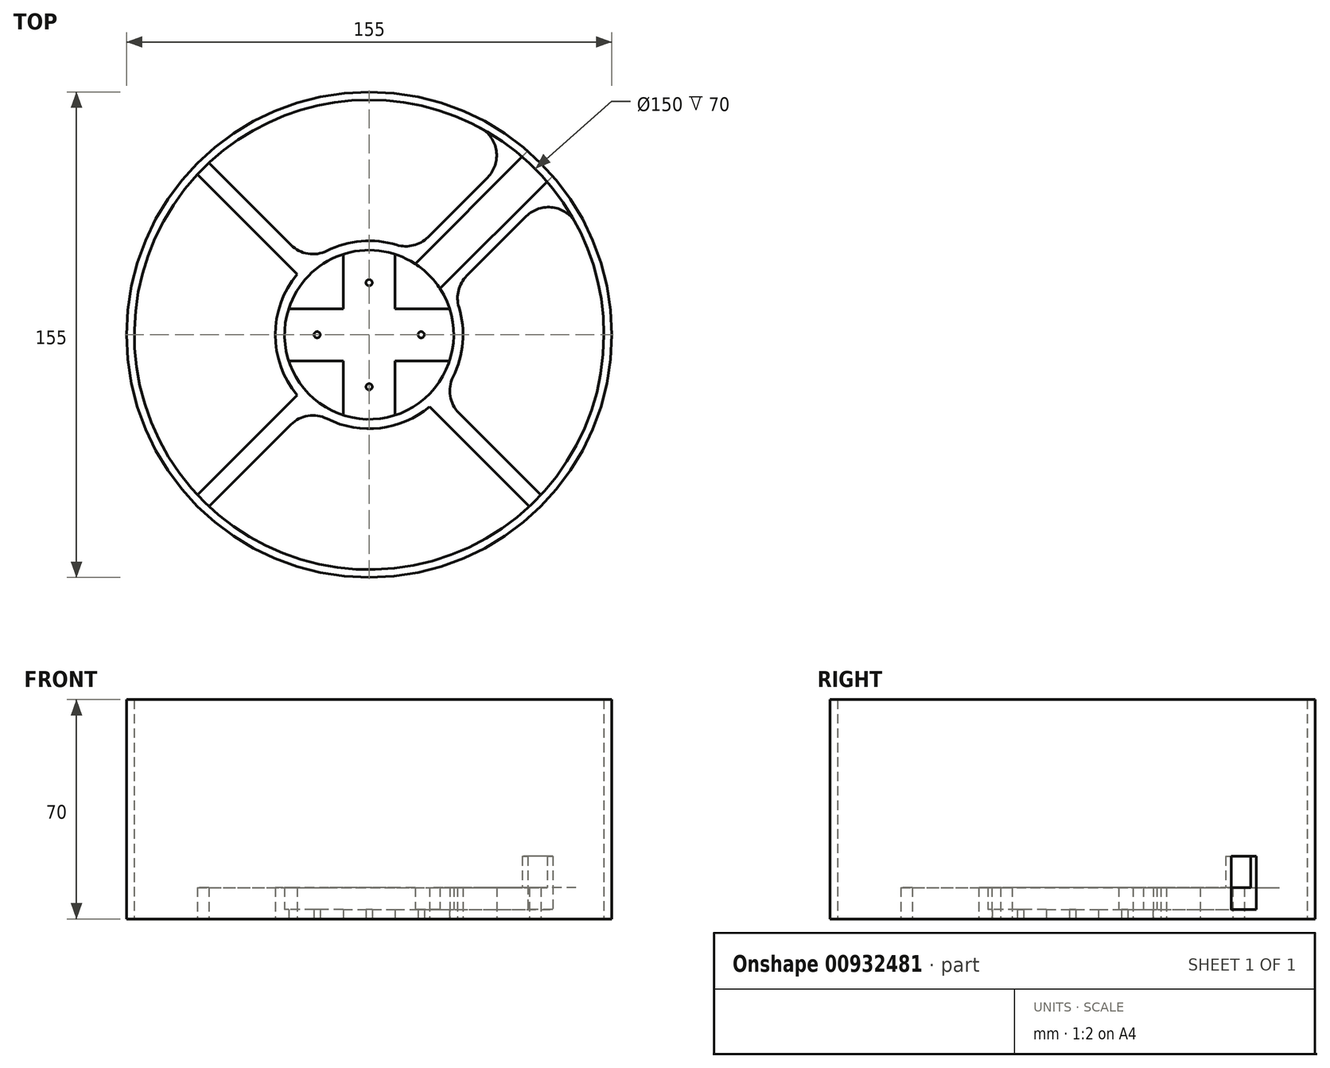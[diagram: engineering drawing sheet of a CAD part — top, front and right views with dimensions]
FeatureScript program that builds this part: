
annotation { "Feature Type Name" : "Feature", "Feature Type Description" : "" }
export const myFeature = defineFeature(function(context is Context, id is Id, definition is map)
    precondition{}
    {
        {
            var Q0;
            Q0=qCreatedBy(makeId("Top.planeOp"),FACE);
            var sketch = newSketch(context, id + "F0", { "sketchPlane" : qUnion([Q0])});
            skCircle(sketch, "E0", {"center": v(0, 0) * mm, "radius": 77.5 * mm});
            skCircle(sketch, "E1", {"center": v(0, 0) * mm, "radius": 75 * mm});
            skSolve(sketch);
        }
        {
            var Q0;
            Q0=qSketchRegion(id+"F0",true);
            var Q1;
            Q1=makeQuery(id+"F0.imprint","IMPRINT",FACE,{"disambiguationData":[TD([[makeQuery(id+"F0.imprint","IMPRINT",EDGE,{"derivedFrom":sQuery(id+"F0.wireOp",EDGE,"E0")}),1.0]])]});
            extrude(context, id + "F1", {"entities" : qUnion([Q0, Q1]), "depth" : 70 * mm, "offsetDistance" : 25 * mm});
        }
        {
            var Q0;
            Q0=qCreatedBy(makeId("Top.planeOp"),FACE);
            var sketch = newSketch(context, id + "F2", { "sketchPlane" : qUnion([Q0])});
            skPoint(sketch, "E2.middle", {"position": v(0, 0) * mm});
            skCircle(sketch, "E3", {"center": v(0, -16.62) * mm, "radius": 1 * mm});
            skCircle(sketch, "E4.0.1.0", {"center": v(16.62, 0) * mm, "radius": 1 * mm});
            skCircle(sketch, "E4.1.0.0", {"center": v(-16.62, 0) * mm, "radius": 1 * mm});
            skCircle(sketch, "E4.1.1.0", {"center": v(0, 16.62) * mm, "radius": 1 * mm});
            skLineSegment(sketch, "E4.direction1", {"start": v(0, -16.62) * mm, "end": v(-16.62, 0) * mm, "construction": true});
            skLineSegment(sketch, "E4.direction2", {"start": v(0, -16.62) * mm, "end": v(16.62, 0) * mm, "construction": true});
            skArc(sketch, "E5", {"start": v(28.83, -8.3) * mm, "mid": v(30, 0) * mm, "end": v(28.83, 8.3) * mm});
            skLineSegment(sketch, "E6", {"start": v(16.62, 0) * mm, "end": v(-16.62, 0) * mm});
            skLineSegment(sketch, "E7", {"start": v(8.3, 8.3) * mm, "end": v(28.83, 8.3) * mm});
            skLineSegment(sketch, "E8.MirrorCS", {"start": v(8.3, 8.3) * mm, "end": v(8.3, 28.83) * mm});
            skLineSegment(sketch, "E9.1.0", {"start": v(-8.3, 8.3) * mm, "end": v(-28.83, 8.3) * mm});
            skLineSegment(sketch, "E9.1.1", {"start": v(-8.3, 8.3) * mm, "end": v(-8.3, 28.83) * mm});
            skLineSegment(sketch, "E9.2.0", {"start": v(-8.3, -8.3) * mm, "end": v(-8.3, -28.83) * mm});
            skLineSegment(sketch, "E9.2.1", {"start": v(-8.3, -8.3) * mm, "end": v(-28.83, -8.3) * mm});
            skLineSegment(sketch, "E10.1.3.0", {"start": v(8.3, -8.3) * mm, "end": v(28.83, -8.3) * mm});
            skLineSegment(sketch, "E10.3.3.0", {"start": v(8.3, -8.3) * mm, "end": v(8.3, -28.83) * mm});
            skArc(sketch, "E11.trimOffspring", {"start": v(8.3, 28.83) * mm, "mid": v(0, 30) * mm, "end": v(-8.3, 28.83) * mm});
            skArc(sketch, "E12.trimOffspring", {"start": v(-28.83, 8.3) * mm, "mid": v(-30, 0) * mm, "end": v(-28.83, -8.3) * mm});
            skArc(sketch, "E13.trimOffspring", {"start": v(-8.3, -28.83) * mm, "mid": v(0, -30) * mm, "end": v(8.3, -28.83) * mm});
            skLineSegment(sketch, "E14.0", {"start": v(-8.3, -8.3) * mm, "end": v(0, -16.62) * mm, "construction": true});
            skLineSegment(sketch, "E14.1", {"start": v(-8.3, -8.3) * mm, "end": v(0, 0) * mm, "construction": true});
            skLineSegment(sketch, "E15.0", {"start": v(0, 16.62) * mm, "end": v(8.3, 8.3) * mm, "construction": true});
            skSolve(sketch);
        }
        {
            var Q0;
            Q0=qSketchRegion(id+"F2",true);
            extrude(context, id + "F3", {"entities" : qUnion([Q0]), "depth" : 3 * mm, "offsetDistance" : 25 * mm});
        }
        {
            var Q0;
            Q0=qCreatedBy(makeId("Top.planeOp"),FACE);
            var sketch = newSketch(context, id + "F4", { "sketchPlane" : qUnion([Q0])});
            skCircle(sketch, "E16", {"center": v(0, 0) * mm, "radius": 30 * mm});
            skCircle(sketch, "E17.0", {"center": v(0, 0) * mm, "radius": 27 * mm});
            skSolve(sketch);
        }
        {
            var Q0;
            Q0=qSketchRegion(id+"F4",true);
            extrude(context, id + "F5", {"entities" : qUnion([Q0]), "operationType" : NewBodyOperationType.ADD, "depth" : 10 * mm, "offsetDistance" : 25 * mm});
        }
        {
            var Q0;
            Q0=qCreatedBy(makeId("Top.planeOp"),FACE);
            var sketch = newSketch(context, id + "F6", { "sketchPlane" : qUnion([Q0])});
            skArc(sketch, "E18", {"start": v(-22.96, -19.3) * mm, "mid": v(-21.21, -21.21) * mm, "end": v(-19.3, -22.96) * mm});
            skArc(sketch, "E19", {"start": v(-54.83, -51.18) * mm, "mid": v(-53.03, -53.03) * mm, "end": v(-51.18, -54.83) * mm});
            skLineSegment(sketch, "E20", {"start": v(-51.18, -54.83) * mm, "end": v(-19.3, -22.96) * mm});
            skLineSegment(sketch, "E21.MirrorCS", {"start": v(-54.83, -51.18) * mm, "end": v(-22.96, -19.3) * mm});
            skPoint(sketch, "E22.center", {"position": v(-2.42, -0.16) * mm});
            skPoint(sketch, "E23", {"position": v(-53.03, -53.03) * mm});
            skPoint(sketch, "E24", {"position": v(-21.21, -21.21) * mm});
            skLineSegment(sketch, "E25", {"start": v(-53.03, -53.03) * mm, "end": v(-21.21, -21.21) * mm, "construction": true});
            skLineSegment(sketch, "E26", {"start": v(-54.83, -51.18) * mm, "end": v(-51.18, -54.83) * mm});
            skLineSegment(sketch, "E27", {"start": v(-22.96, -19.3) * mm, "end": v(-19.3, -22.96) * mm});
            skLineSegment(sketch, "E28", {"start": v(-21.21, -21.21) * mm, "end": v(0, 0) * mm, "construction": true});
            skLineSegment(sketch, "E29.1.0", {"start": v(54.83, -51.18) * mm, "end": v(22.96, -19.3) * mm});
            skLineSegment(sketch, "E29.1.1", {"start": v(53.03, -53.03) * mm, "end": v(21.21, -21.21) * mm, "construction": true});
            skLineSegment(sketch, "E29.1.2", {"start": v(51.18, -54.83) * mm, "end": v(19.3, -22.96) * mm});
            skArc(sketch, "E29.1.3", {"start": v(51.18, -54.83) * mm, "mid": v(53.03, -53.03) * mm, "end": v(54.83, -51.18) * mm});
            skArc(sketch, "E29.1.4", {"start": v(19.3, -22.96) * mm, "mid": v(21.21, -21.21) * mm, "end": v(22.96, -19.3) * mm});
            skLineSegment(sketch, "E29.1.5", {"start": v(21.21, -21.21) * mm, "end": v(0, 0) * mm, "construction": true});
            skLineSegment(sketch, "E30.3.3.0", {"start": v(-53.03, 53.03) * mm, "end": v(-21.21, 21.21) * mm, "construction": true});
            skLineSegment(sketch, "E30.4.3.0", {"start": v(-54.83, 51.18) * mm, "end": v(-22.96, 19.3) * mm});
            skLineSegment(sketch, "E30.6.3.0", {"start": v(-51.18, 54.83) * mm, "end": v(-19.3, 22.96) * mm});
            skArc(sketch, "E30.9.3.0", {"start": v(-51.18, 54.83) * mm, "mid": v(-53.03, 53.03) * mm, "end": v(-54.83, 51.18) * mm});
            skArc(sketch, "E30.13.3.0", {"start": v(-19.3, 22.96) * mm, "mid": v(-21.21, 21.21) * mm, "end": v(-22.96, 19.3) * mm});
            skLineSegment(sketch, "E30.17.3.0", {"start": v(-21.21, 21.21) * mm, "end": v(0, 0) * mm, "construction": true});
            skLineSegment(sketch, "E31", {"start": v(26.42, 14.02) * mm, "end": v(59.73, 47.33) * mm});
            skLineSegment(sketch, "E32.MirrorCS", {"start": v(14.02, 26.42) * mm, "end": v(47.33, 59.73) * mm});
            skLineSegment(sketch, "E33", {"start": v(26.42, 14.02) * mm, "end": v(14.02, 26.42) * mm});
            skLineSegment(sketch, "E34", {"start": v(59.73, 47.33) * mm, "end": v(47.33, 59.73) * mm});
            skSolve(sketch);
        }
        {
            var Q0;
            Q0=qSketchRegion(id+"F6",true);
            extrude(context, id + "F7", {"entities" : qUnion([Q0]), "depth" : 10 * mm, "offsetDistance" : 25 * mm});
        }
        {
            var Q0;
            Q0=makeQuery(id+"F7.opExtrude","CAP_FACE",FACE,{"disambiguationData":[OSD([sQuery(id+"F6.wireOp",EDGE,"E31"),sQuery(id+"F6.wireOp",EDGE,"E32.MirrorCS"),sQuery(id+"F6.wireOp",EDGE,"E33"),sQuery(id+"F6.wireOp",EDGE,"E34")])],"isStart":false});
            cPlane(context, id + "F8", {"entities" : qUnion([Q0]), "cplaneType" : CPlaneType.OFFSET, "offset" : 10 * mm, "width" : 150 * mm, "height" : 150 * mm});
        }
        {
            var Q0;
            Q0=qCreatedBy(id+"F8.planeOp",FACE);
            var sketch = newSketch(context, id + "F9", { "sketchPlane" : qUnion([Q0])});
            skLineSegment(sketch, "E35", {"start": v(21.24, 13.28) * mm, "end": v(13.28, 21.24) * mm});
            skLineSegment(sketch, "E36", {"start": v(60.56, 52.6) * mm, "end": v(52.6, 60.56) * mm});
            skLineSegment(sketch, "E37.trimOffspring", {"start": v(13.28, 21.24) * mm, "end": v(52.6, 60.56) * mm});
            skLineSegment(sketch, "E38.trimOffspring", {"start": v(21.24, 13.28) * mm, "end": v(60.56, 52.6) * mm});
            skSolve(sketch);
        }
        {
            var Q0;
            Q0 = qSketchRegion(id + "F9", true);
            var Q1;
            Q1=qCreatedBy(makeId("Top.planeOp"),FACE);
            extrude(context, id + "F10", {"entities" : qUnion([Q0]), "operationType" : NewBodyOperationType.REMOVE, "oppositeDirection" : true, "depth" : 17 * mm, "endBoundEntityFace" : qUnion([Q1]), "offsetDistance" : 25 * mm});
        }
        {
            var Q0;
            Q0=makeQuery(id+"F3.opExtrude","SWEPT_BODY",BODY,{"disambiguationData":[OSD([sQuery(id+"F2.wireOp",EDGE,"E3"),sQuery(id+"F2.wireOp",EDGE,"E4.0.1.0"),sQuery(id+"F2.wireOp",EDGE,"E4.1.0.0"),sQuery(id+"F2.wireOp",EDGE,"E4.1.1.0"),sQuery(id+"F2.wireOp",EDGE,"E5"),sQuery(id+"F2.wireOp",EDGE,"E8.MirrorCS"),sQuery(id+"F2.wireOp",EDGE,"E7"),sQuery(id+"F2.wireOp",EDGE,"E9.1.0"),sQuery(id+"F2.wireOp",EDGE,"E9.1.1"),sQuery(id+"F2.wireOp",EDGE,"E9.2.0"),sQuery(id+"F2.wireOp",EDGE,"E9.2.1"),sQuery(id+"F2.wireOp",EDGE,"E10.1.3.0"),sQuery(id+"F2.wireOp",EDGE,"E10.3.3.0"),sQuery(id+"F2.wireOp",EDGE,"E11.trimOffspring"),sQuery(id+"F2.wireOp",EDGE,"E12.trimOffspring"),sQuery(id+"F2.wireOp",EDGE,"E13.trimOffspring")])]});
            var Q1;
            Q1=makeQuery(id+"F7.opExtrude","SWEPT_BODY",BODY,{"disambiguationData":[OSD([sQuery(id+"F6.wireOp",EDGE,"E19"),sQuery(id+"F6.wireOp",EDGE,"E20"),sQuery(id+"F6.wireOp",EDGE,"E21.MirrorCS"),sQuery(id+"F6.wireOp",EDGE,"E27")])]});
            var Q2;
            Q2=makeQuery(id+"F7.opExtrude","SWEPT_BODY",BODY,{"disambiguationData":[OSD([sQuery(id+"F6.wireOp",EDGE,"E29.1.0"),sQuery(id+"F6.wireOp",EDGE,"E29.1.2"),sQuery(id+"F6.wireOp",EDGE,"E29.1.3"),sQuery(id+"F6.wireOp",EDGE,"E29.1.4")])]});
            var Q3;
            Q3=makeQuery(id+"F7.opExtrude","SWEPT_BODY",BODY,{"disambiguationData":[OSD([sQuery(id+"F6.wireOp",EDGE,"E30.4.3.0"),sQuery(id+"F6.wireOp",EDGE,"E30.6.3.0"),sQuery(id+"F6.wireOp",EDGE,"E30.9.3.0"),sQuery(id+"F6.wireOp",EDGE,"E30.13.3.0")])]});
            var Q4;
            Q4=makeQuery(id+"F7.opExtrude","SWEPT_BODY",BODY,{"disambiguationData":[OSD([sQuery(id+"F6.wireOp",EDGE,"E31"),sQuery(id+"F6.wireOp",EDGE,"E32.MirrorCS"),sQuery(id+"F6.wireOp",EDGE,"E33"),sQuery(id+"F6.wireOp",EDGE,"E34")])]});
            var Q5;
            Q5=makeQuery(id+"F1.opExtrude","SWEPT_BODY",BODY,{"disambiguationData":[OSD([sQuery(id+"F0.wireOp",EDGE,"E0"),sQuery(id+"F0.wireOp",EDGE,"E1")])]});
            booleanBodies(context, id + "F11", {"operationType" : BooleanOperationType.UNION, "tools" : qUnion([Q0, Q1, Q2, Q3, Q4, Q5])});
        }
        {
            var Q0;
            Q0=makeQuery(id+"F7.opExtrude","SWEPT_EDGE",EDGE,{"disambiguationData":[OSD([sQuery(id+"F6.wireOp",EDGE,"E30.6.3.0"),sQuery(id+"F6.wireOp",EDGE,"E30.9.3.0")])]});
            var Q1;
            Q1=makeQuery(id+"F7.opExtrude","SWEPT_EDGE",EDGE,{"disambiguationData":[OSD([sQuery(id+"F6.wireOp",EDGE,"E30.4.3.0"),sQuery(id+"F6.wireOp",EDGE,"E30.9.3.0")])]});
            var Q2;
            Q2=makeQuery(id+"F11.opBoolean","INTERSECT",EDGE,{"derivedFrom":[makeQuery(id+"F7.opExtrude","SWEPT_FACE",FACE,{"disambiguationData":[OSD([sQuery(id+"F6.wireOp",EDGE,"E31")])]}),makeQuery(id+"F1.opExtrude","SWEPT_FACE",FACE,{"disambiguationData":[OSD([sQuery(id+"F0.wireOp",EDGE,"E1")])]})]});
            var Q3;
            Q3=makeQuery(id+"F11.opBoolean","INTERSECT",EDGE,{"derivedFrom":[makeQuery(id+"F7.opExtrude","SWEPT_FACE",FACE,{"disambiguationData":[OSD([sQuery(id+"F6.wireOp",EDGE,"E32.MirrorCS")])]}),makeQuery(id+"F1.opExtrude","SWEPT_FACE",FACE,{"disambiguationData":[OSD([sQuery(id+"F0.wireOp",EDGE,"E1")])]})]});
            var Q4;
            Q4=makeQuery(id+"F7.opExtrude","SWEPT_EDGE",EDGE,{"disambiguationData":[OSD([sQuery(id+"F6.wireOp",EDGE,"E29.1.2"),sQuery(id+"F6.wireOp",EDGE,"E29.1.3")])]});
            var Q5;
            Q5=makeQuery(id+"F7.opExtrude","SWEPT_EDGE",EDGE,{"disambiguationData":[OSD([sQuery(id+"F6.wireOp",EDGE,"E29.1.0"),sQuery(id+"F6.wireOp",EDGE,"E29.1.3")])]});
            var Q6;
            Q6=makeQuery(id+"F7.opExtrude","SWEPT_EDGE",EDGE,{"disambiguationData":[OSD([sQuery(id+"F6.wireOp",EDGE,"E19"),sQuery(id+"F6.wireOp",EDGE,"E20"),sQuery(id+"F6.wireOp",EDGE,"E26")])]});
            var Q7;
            Q7=makeQuery(id+"F7.opExtrude","SWEPT_EDGE",EDGE,{"disambiguationData":[OSD([sQuery(id+"F6.wireOp",EDGE,"E19"),sQuery(id+"F6.wireOp",EDGE,"E21.MirrorCS"),sQuery(id+"F6.wireOp",EDGE,"E26")])]});
            var Q8;
            Q8=makeQuery(id+"F7.opExtrude","SWEPT_EDGE",EDGE,{"disambiguationData":[OSD([sQuery(id+"F6.wireOp",EDGE,"E18"),sQuery(id+"F6.wireOp",EDGE,"E21.MirrorCS"),sQuery(id+"F6.wireOp",EDGE,"E27")])]});
            var Q9;
            Q9=makeQuery(id+"F7.opExtrude","SWEPT_EDGE",EDGE,{"disambiguationData":[OSD([sQuery(id+"F6.wireOp",EDGE,"E18"),sQuery(id+"F6.wireOp",EDGE,"E20"),sQuery(id+"F6.wireOp",EDGE,"E27")])]});
            var Q10;
            Q10=makeQuery(id+"F7.opExtrude","SWEPT_EDGE",EDGE,{"disambiguationData":[OSD([sQuery(id+"F6.wireOp",EDGE,"E29.1.0"),sQuery(id+"F6.wireOp",EDGE,"E29.1.4")])]});
            var Q11;
            Q11=makeQuery(id+"F11.opBoolean","INTERSECT",EDGE,{"derivedFrom":[makeQuery(id+"F7.opExtrude","SWEPT_FACE",FACE,{"disambiguationData":[OSD([sQuery(id+"F6.wireOp",EDGE,"E32.MirrorCS")])]}),makeQuery(id+"F5.boolean.opBoolean","MERGE",FACE,{"derivedFrom":[makeQuery(id+"F3.opExtrude","SWEPT_FACE",FACE,{"disambiguationData":[OSD([sQuery(id+"F2.wireOp",EDGE,"E5")])]}),makeQuery(id+"F3.opExtrude","SWEPT_FACE",FACE,{"disambiguationData":[OSD([sQuery(id+"F2.wireOp",EDGE,"E11.trimOffspring")])]}),makeQuery(id+"F3.opExtrude","SWEPT_FACE",FACE,{"disambiguationData":[OSD([sQuery(id+"F2.wireOp",EDGE,"E12.trimOffspring")])]}),makeQuery(id+"F3.opExtrude","SWEPT_FACE",FACE,{"disambiguationData":[OSD([sQuery(id+"F2.wireOp",EDGE,"E13.trimOffspring")])]}),makeQuery(id+"F5.opExtrude","SWEPT_FACE",FACE,{"disambiguationData":[OSD([sQuery(id+"F4.wireOp",EDGE,"E16")])]})]})]});
            var Q12;
            Q12=makeQuery(id+"F11.opBoolean","INTERSECT",EDGE,{"derivedFrom":[makeQuery(id+"F7.opExtrude","SWEPT_FACE",FACE,{"disambiguationData":[OSD([sQuery(id+"F6.wireOp",EDGE,"E31")])]}),makeQuery(id+"F5.boolean.opBoolean","MERGE",FACE,{"derivedFrom":[makeQuery(id+"F3.opExtrude","SWEPT_FACE",FACE,{"disambiguationData":[OSD([sQuery(id+"F2.wireOp",EDGE,"E5")])]}),makeQuery(id+"F3.opExtrude","SWEPT_FACE",FACE,{"disambiguationData":[OSD([sQuery(id+"F2.wireOp",EDGE,"E11.trimOffspring")])]}),makeQuery(id+"F3.opExtrude","SWEPT_FACE",FACE,{"disambiguationData":[OSD([sQuery(id+"F2.wireOp",EDGE,"E12.trimOffspring")])]}),makeQuery(id+"F3.opExtrude","SWEPT_FACE",FACE,{"disambiguationData":[OSD([sQuery(id+"F2.wireOp",EDGE,"E13.trimOffspring")])]}),makeQuery(id+"F5.opExtrude","SWEPT_FACE",FACE,{"disambiguationData":[OSD([sQuery(id+"F4.wireOp",EDGE,"E16")])]})]})]});
            var Q13;
            Q13=makeQuery(id+"F7.opExtrude","SWEPT_EDGE",EDGE,{"disambiguationData":[OSD([sQuery(id+"F6.wireOp",EDGE,"E30.6.3.0"),sQuery(id+"F6.wireOp",EDGE,"E30.13.3.0")])]});
            var Q14;
            Q14=makeQuery(id+"F7.opExtrude","SWEPT_EDGE",EDGE,{"disambiguationData":[OSD([sQuery(id+"F6.wireOp",EDGE,"E30.4.3.0"),sQuery(id+"F6.wireOp",EDGE,"E30.13.3.0")])]});
            fillet(context, id + "F12", {"entities" : qUnion([Q0, Q1, Q2, Q3, Q4, Q5, Q6, Q7, Q8, Q9, Q10, Q11, Q12, Q13, Q14]), "radius" : 10 * mm, "tangentPropagation" : true, "allowEdgeOverflow" : false});
        }
    });
